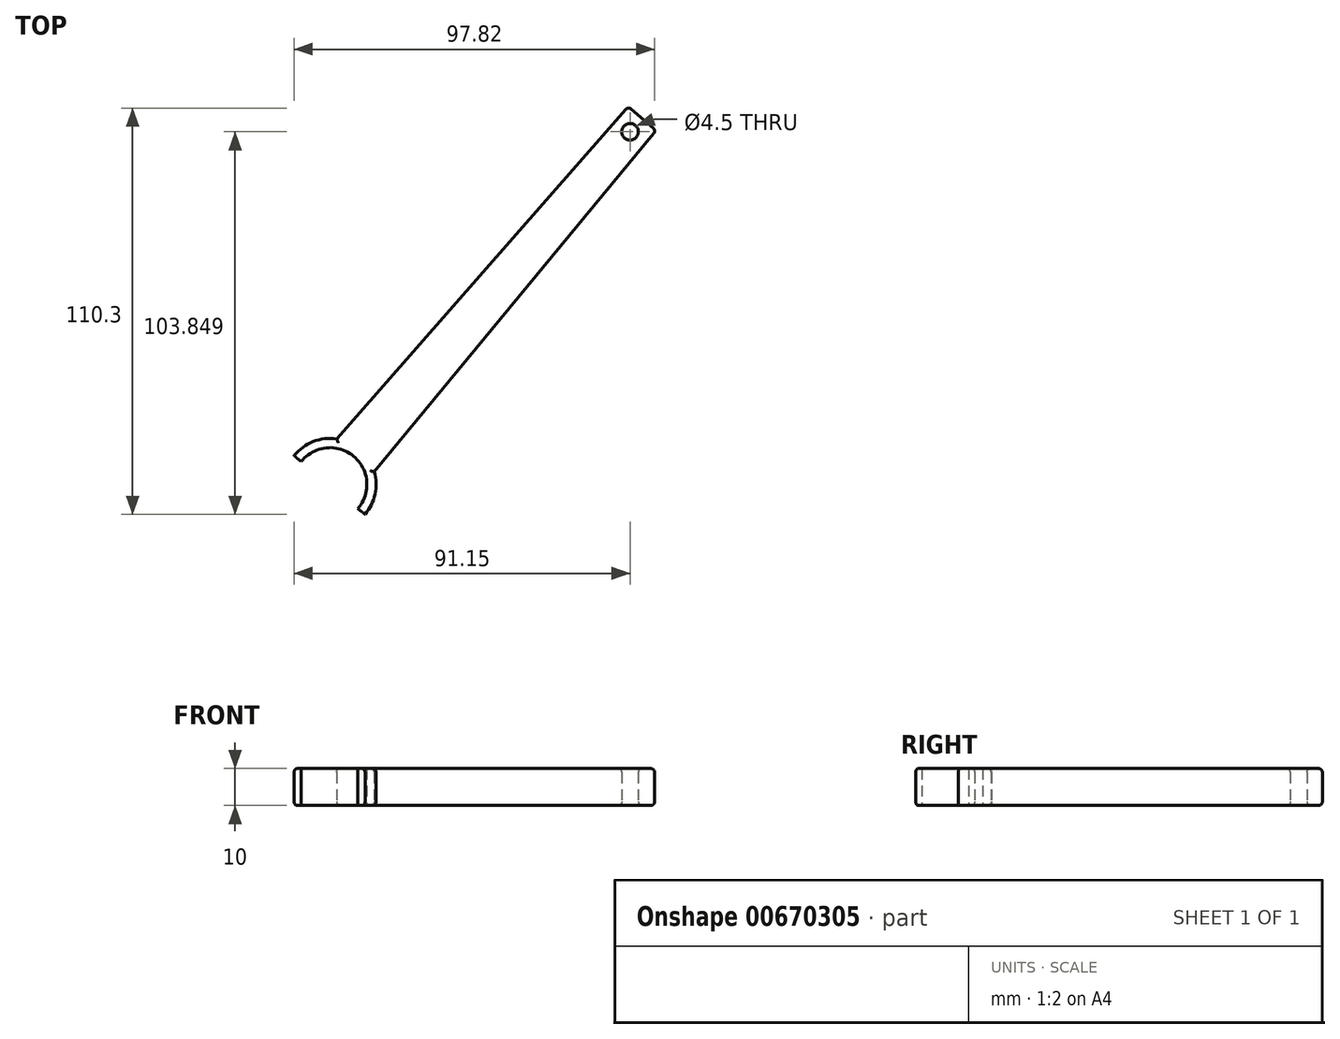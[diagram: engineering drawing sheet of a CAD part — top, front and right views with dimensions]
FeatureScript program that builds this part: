
annotation { "Feature Type Name" : "Feature", "Feature Type Description" : "" }
export const myFeature = defineFeature(function(context is Context, id is Id, definition is map)
    precondition{}
    {
        {
            var Q0;
            Q0=qCreatedBy(makeId("Top.planeOp"),FACE);
            var sketch = newSketch(context, id + "F0", { "sketchPlane" : qUnion([Q0])});
            skCircle(sketch, "E0", {"center": v(0, 0) * mm, "radius": 12.5 * mm});
            skCircle(sketch, "E1", {"center": v(0, 0) * mm, "radius": 10 * mm});
            skLineSegment(sketch, "E2", {"start": v(1.84, 12.36) * mm, "end": v(80.95, 102.6) * mm});
            skLineSegment(sketch, "E3", {"start": v(80.95, 102.6) * mm, "end": v(88.47, 96) * mm});
            skLineSegment(sketch, "E4", {"start": v(88.47, 96) * mm, "end": v(12.01, 3.46) * mm});
            skLineSegment(sketch, "E5", {"start": v(-9.74, 7.84) * mm, "end": v(9.5, -8.12) * mm});
            skCircle(sketch, "E6", {"center": v(81.4, 95.73) * mm, "radius": 2.25 * mm});
            skSolve(sketch);
        }
        {
            var Q0;
            {var subQ0=sQuery(id+"F0.wireOp",EDGE,"E0");var subQ4=makeQuery(id+"F0.imprint","INTERSECT",VERTEX,{"derivedFrom":[subQ0,sQuery(id+"F0.wireOp",EDGE,"E2")]});Q0=makeQuery(id+"F0.imprint","IMPRINT",FACE,{"disambiguationData":[TD([[makeQuery(id+"F0.imprint","IMPRINT",EDGE,{"disambiguationData":[TD([[subQ4,1.0]])],"derivedFrom":subQ0}),1.0]])]});}
            var Q1;
            {var subQ1=sQuery(id+"F0.wireOp",EDGE,"E2");Q1=makeQuery(id+"F0.imprint","IMPRINT",FACE,{"disambiguationData":[TD([[makeQuery(id+"F0.imprint","IMPRINT",EDGE,{"derivedFrom":subQ1}),-1.0]])]});}
            extrude(context, id + "F1", {"entities" : qUnion([Q0, Q1]), "depth" : 10 * mm, "offsetDistance" : 25.4 * mm});
        }
        {
            var Q0;
            Q0=makeQuery(id+"F1.opExtrude","CAP_EDGE",EDGE,{"disambiguationData":[OSD([sQuery(id+"F0.wireOp",EDGE,"E2")])],"isStart":false});
            var Q1;
            {var subQ0=sQuery(id+"F0.wireOp",EDGE,"E0");Q1=makeQuery(id+"F1.opExtrude","CAP_EDGE",EDGE,{"disambiguationData":[OSD([subQ0]),TDD([makeQuery(id+"F0.imprint","IMPRINT",EDGE,{"disambiguationData":[TD([[makeQuery(id+"F0.imprint","INTERSECT",VERTEX,{"derivedFrom":[subQ0,sQuery(id+"F0.wireOp",EDGE,"E4")]}),1.0]])],"derivedFrom":subQ0})])],"isStart":false});}
            var Q2;
            Q2=makeQuery(id+"F1.opExtrude","CAP_EDGE",EDGE,{"disambiguationData":[OSD([sQuery(id+"F0.wireOp",EDGE,"E4")])],"isStart":false});
            var Q3;
            {var subQ0=sQuery(id+"F0.wireOp",EDGE,"E0");Q3=makeQuery(id+"F1.opExtrude","CAP_EDGE",EDGE,{"disambiguationData":[OSD([subQ0]),TDD([makeQuery(id+"F0.imprint","IMPRINT",EDGE,{"disambiguationData":[TD([[makeQuery(id+"F0.imprint","INTERSECT",VERTEX,{"derivedFrom":[subQ0,sQuery(id+"F0.wireOp",EDGE,"E2")]}),-1.0]])],"derivedFrom":subQ0})])],"isStart":false});}
            var Q4;
            {var subQ0=sQuery(id+"F0.wireOp",EDGE,"E0");Q4=makeQuery(id+"F1.opExtrude","CAP_EDGE",EDGE,{"disambiguationData":[OSD([subQ0]),TDD([makeQuery(id+"F0.imprint","IMPRINT",EDGE,{"disambiguationData":[TD([[makeQuery(id+"F0.imprint","INTERSECT",VERTEX,{"derivedFrom":[subQ0,sQuery(id+"F0.wireOp",EDGE,"E4")]}),1.0]])],"derivedFrom":subQ0})])],"isStart":true});}
            var Q5;
            {var subQ0=sQuery(id+"F0.wireOp",EDGE,"E0");Q5=makeQuery(id+"F1.opExtrude","CAP_EDGE",EDGE,{"disambiguationData":[OSD([subQ0]),TDD([makeQuery(id+"F0.imprint","IMPRINT",EDGE,{"disambiguationData":[TD([[makeQuery(id+"F0.imprint","INTERSECT",VERTEX,{"derivedFrom":[subQ0,sQuery(id+"F0.wireOp",EDGE,"E2")]}),-1.0]])],"derivedFrom":subQ0})])],"isStart":true});}
            var Q6;
            Q6=makeQuery(id+"F1.opExtrude","CAP_EDGE",EDGE,{"disambiguationData":[OSD([sQuery(id+"F0.wireOp",EDGE,"E4")])],"isStart":true});
            var Q7;
            Q7=makeQuery(id+"F1.opExtrude","CAP_EDGE",EDGE,{"disambiguationData":[OSD([sQuery(id+"F0.wireOp",EDGE,"E2")])],"isStart":true});
            var Q8;
            Q8=makeQuery(id+"F1.opExtrude","CAP_EDGE",EDGE,{"disambiguationData":[OSD([sQuery(id+"F0.wireOp",EDGE,"E6")])],"isStart":true});
            var Q9;
            Q9=makeQuery(id+"F1.opExtrude","CAP_EDGE",EDGE,{"disambiguationData":[OSD([sQuery(id+"F0.wireOp",EDGE,"E3")])],"isStart":true});
            var Q10;
            Q10=makeQuery(id+"F1.opExtrude","CAP_EDGE",EDGE,{"disambiguationData":[OSD([sQuery(id+"F0.wireOp",EDGE,"E6")])],"isStart":false});
            var Q11;
            Q11=makeQuery(id+"F1.opExtrude","SWEPT_FACE",FACE,{"disambiguationData":[OSD([sQuery(id+"F0.wireOp",EDGE,"E3")])]});
            fillet(context, id + "F2", {"entities" : qUnion([Q0, Q1, Q2, Q3, Q4, Q5, Q6, Q7, Q8, Q9, Q10, Q11]), "radius" : 1 * mm, "tangentPropagation" : true, "allowEdgeOverflow" : false});
        }
    });
